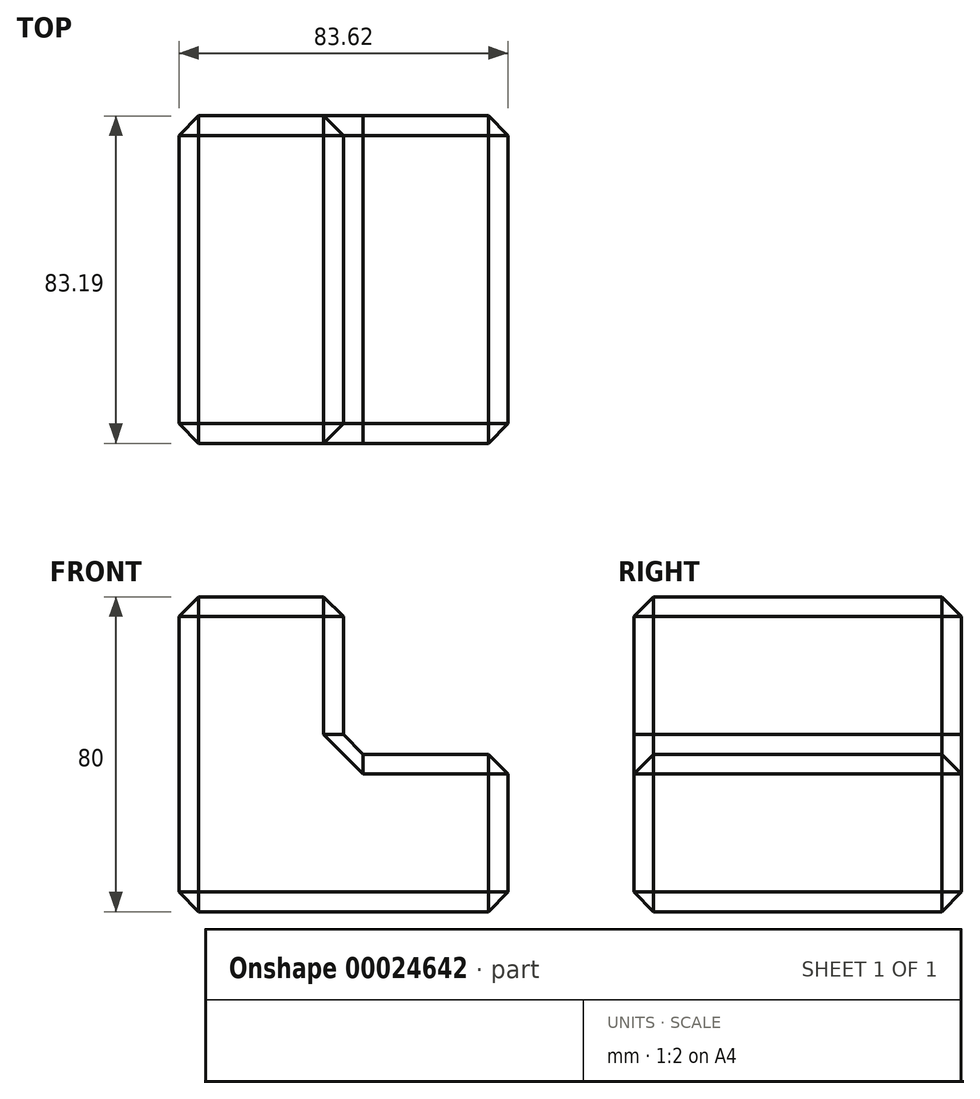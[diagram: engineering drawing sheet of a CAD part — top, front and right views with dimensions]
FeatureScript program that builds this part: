
annotation { "Feature Type Name" : "Feature", "Feature Type Description" : "" }
export const myFeature = defineFeature(function(context is Context, id is Id, definition is map)
    precondition{}
    {
        {
            var Q0;
            Q0=qCreatedBy(makeId("Top.planeOp"),FACE);
            var sketch = newSketch(context, id + "F0", { "sketchPlane" : qUnion([Q0])});
            skLineSegment(sketch, "E0.bottom", {"start": v(-59.13, -45.93) * mm, "end": v(24.5, -45.93) * mm});
            skLineSegment(sketch, "E0.top", {"start": v(-59.13, 37.26) * mm, "end": v(24.5, 37.26) * mm});
            skLineSegment(sketch, "E0.left", {"start": v(-59.13, -45.93) * mm, "end": v(-59.13, 37.26) * mm});
            skLineSegment(sketch, "E0.right", {"start": v(24.5, -45.93) * mm, "end": v(24.5, 37.26) * mm});
            skSolve(sketch);
        }
        {
            var Q0;
            Q0=makeQuery(id+"F0.imprint","IMPRINT",FACE,{"disambiguationData":[TD([[makeQuery(id+"F0.imprint","IMPRINT",EDGE,{"derivedFrom":sQuery(id+"F0.wireOp",EDGE,"E0.bottom")}),1.0]])]});
            extrude(context, id + "F1", {"entities" : qUnion([Q0]), "depth" : 40 * mm});
        }
        {
            var Q0;
            Q0=makeQuery(id+"F1.opExtrude","CAP_FACE",FACE,{"disambiguationData":[OSD([sQuery(id+"F0.wireOp",EDGE,"E0.bottom"),sQuery(id+"F0.wireOp",EDGE,"E0.top"),sQuery(id+"F0.wireOp",EDGE,"E0.left"),sQuery(id+"F0.wireOp",EDGE,"E0.right")])],"isStart":false});
            var sketch = newSketch(context, id + "F2", { "sketchPlane" : qUnion([Q0])});
            skLineSegment(sketch, "E1", {"start": v(-17.32, 37.26) * mm, "end": v(-17.32, -45.93) * mm});
            skSolve(sketch);
        }
        {
            var Q0;
            {var subQ1=sQuery(id+"F2.wireOp",EDGE,"E1");Q0=makeQuery(id+"F2.imprint","IMPRINT",FACE,{"disambiguationData":[TD([[makeQuery(id+"F2.imprint","IMPRINT",EDGE,{"derivedFrom":subQ1}),-1.0]])]});}
            extrude(context, id + "F3", {"entities" : qUnion([Q0]), "operationType" : NewBodyOperationType.ADD, "depth" : 40 * mm});
        }
        {
            var Q0;
            Q0=makeQuery(id+"F3.opExtrude","CAP_FACE",FACE,{"disambiguationData":[OSD([sQuery(id+"F0.wireOp",EDGE,"E0.bottom"),sQuery(id+"F0.wireOp",EDGE,"E0.top"),sQuery(id+"F0.wireOp",EDGE,"E0.left"),sQuery(id+"F2.wireOp",EDGE,"E1")])],"isStart":false});
            var Q1;
            Q1=makeQuery(id+"F1.opExtrude","CAP_FACE",FACE,{"disambiguationData":[OSD([sQuery(id+"F0.wireOp",EDGE,"E0.bottom"),sQuery(id+"F0.wireOp",EDGE,"E0.top"),sQuery(id+"F0.wireOp",EDGE,"E0.left"),sQuery(id+"F0.wireOp",EDGE,"E0.right")])],"isStart":false});
            var Q2;
            {var subQ0=sQuery(id+"F0.wireOp",EDGE,"E0.left");Q2=makeQuery(id+"F3.boolean.opBoolean","MERGE",FACE,{"derivedFrom":[makeQuery(id+"F1.opExtrude","SWEPT_FACE",FACE,{"disambiguationData":[OSD([subQ0])]}),makeQuery(id+"F3.opExtrude","SWEPT_FACE",FACE,{"disambiguationData":[OSD([subQ0])]})]});}
            var Q3;
            {var subQ0=sQuery(id+"F0.wireOp",EDGE,"E0.top");Q3=makeQuery(id+"F3.boolean.opBoolean","MERGE",FACE,{"derivedFrom":[makeQuery(id+"F1.opExtrude","SWEPT_FACE",FACE,{"disambiguationData":[OSD([subQ0])]}),makeQuery(id+"F3.opExtrude","SWEPT_FACE",FACE,{"disambiguationData":[OSD([subQ0])]})]});}
            var Q4;
            Q4=makeQuery(id+"F1.opExtrude","CAP_FACE",FACE,{"disambiguationData":[OSD([sQuery(id+"F0.wireOp",EDGE,"E0.bottom"),sQuery(id+"F0.wireOp",EDGE,"E0.top"),sQuery(id+"F0.wireOp",EDGE,"E0.left"),sQuery(id+"F0.wireOp",EDGE,"E0.right")])],"isStart":true});
            var Q5;
            Q5=makeQuery(id+"F1.opExtrude","SWEPT_FACE",FACE,{"disambiguationData":[OSD([sQuery(id+"F0.wireOp",EDGE,"E0.right")])]});
            chamfer(context, id + "F4", {"entities" : qUnion([Q0, Q1, Q2, Q3, Q4, Q5]), "width" : 5 * mm, "tangentPropagation" : true});
        }
    });
